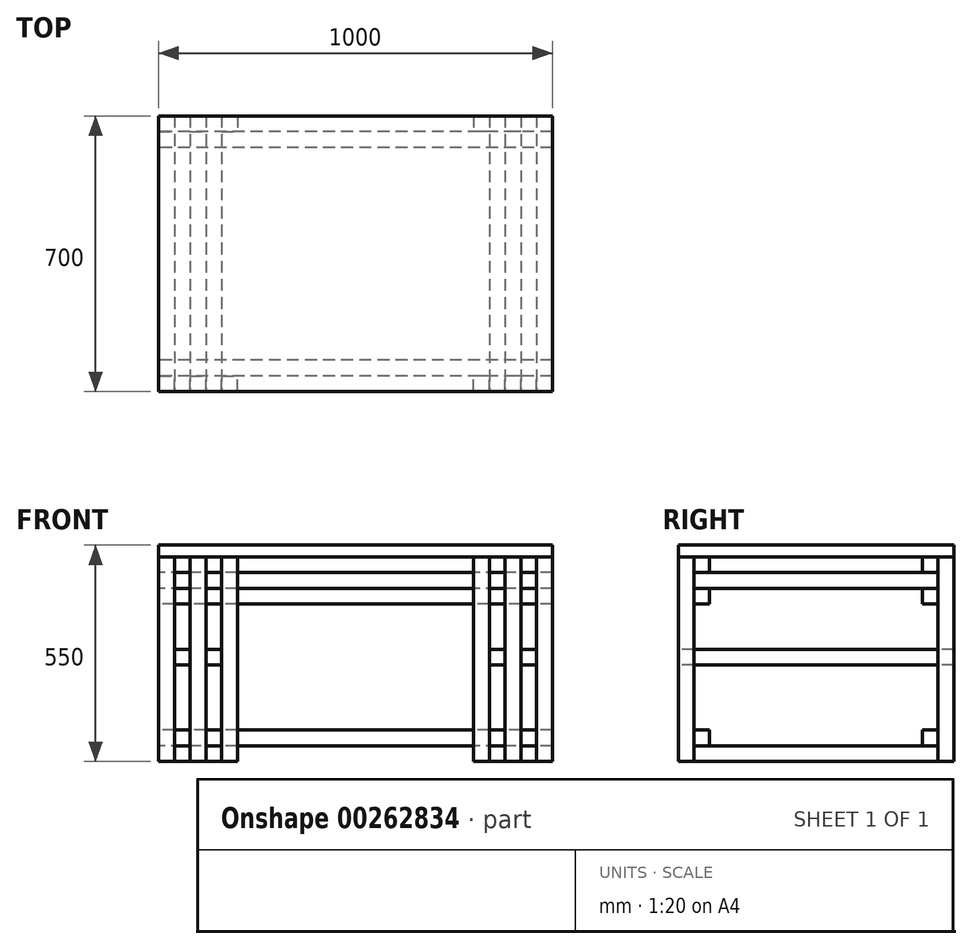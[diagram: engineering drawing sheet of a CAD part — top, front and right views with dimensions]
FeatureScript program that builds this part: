
annotation { "Feature Type Name" : "Feature", "Feature Type Description" : "" }
export const myFeature = defineFeature(function(context is Context, id is Id, definition is map)
    precondition{}
    {
        {
            var Q0;
            Q0=qCreatedBy(makeId("Top.planeOp"),FACE);
            var sketch = newSketch(context, id + "F0", { "sketchPlane" : qUnion([Q0])});
            skLineSegment(sketch, "E0.bottom", {"start": v(500, 350) * mm, "end": v(-500, 350) * mm});
            skLineSegment(sketch, "E0.top", {"start": v(500, -350) * mm, "end": v(-500, -350) * mm});
            skLineSegment(sketch, "E0.left", {"start": v(500, 350) * mm, "end": v(500, -350) * mm});
            skLineSegment(sketch, "E0.right", {"start": v(-500, 350) * mm, "end": v(-500, -350) * mm});
            skPoint(sketch, "E0.middle", {"position": v(0, 0) * mm});
            skSolve(sketch);
        }
        {
            var Q0;
            Q0=makeQuery(id+"F0.imprint","IMPRINT",FACE,{"disambiguationData":[TD([[makeQuery(id+"F0.imprint","IMPRINT",EDGE,{"derivedFrom":sQuery(id+"F0.wireOp",EDGE,"E0.bottom")}),1.0]])]});
            extrude(context, id + "F1", {"entities" : qUnion([Q0]), "depth" : 30 * mm});
        }
        {
            var Q0;
            Q0=makeQuery(id+"F1.opExtrude","CAP_FACE",FACE,{"disambiguationData":[OSD([sQuery(id+"F0.wireOp",EDGE,"E0.bottom"),sQuery(id+"F0.wireOp",EDGE,"E0.top"),sQuery(id+"F0.wireOp",EDGE,"E0.left"),sQuery(id+"F0.wireOp",EDGE,"E0.right")])],"isStart":true});
            var sketch = newSketch(context, id + "F2", { "sketchPlane" : qUnion([Q0])});
            skLineSegment(sketch, "E1.bottom", {"start": v(-500, 350) * mm, "end": v(-460, 350) * mm});
            skLineSegment(sketch, "E1.top", {"start": v(-500, 310) * mm, "end": v(-460, 310) * mm});
            skLineSegment(sketch, "E1.left", {"start": v(-500, 350) * mm, "end": v(-500, 310) * mm});
            skLineSegment(sketch, "E1.right", {"start": v(-460, 350) * mm, "end": v(-460, 310) * mm});
            skLineSegment(sketch, "E2.bottom", {"start": v(-420, 350) * mm, "end": v(-380, 350) * mm});
            skLineSegment(sketch, "E2.top", {"start": v(-420, 310) * mm, "end": v(-380, 310) * mm});
            skLineSegment(sketch, "E2.left", {"start": v(-420, 350) * mm, "end": v(-420, 310) * mm});
            skLineSegment(sketch, "E2.right", {"start": v(-380, 350) * mm, "end": v(-380, 310) * mm});
            skLineSegment(sketch, "E3.bottom", {"start": v(-340, 350) * mm, "end": v(-300, 350) * mm});
            skLineSegment(sketch, "E3.top", {"start": v(-340, 310) * mm, "end": v(-300, 310) * mm});
            skLineSegment(sketch, "E3.left", {"start": v(-340, 350) * mm, "end": v(-340, 310) * mm});
            skLineSegment(sketch, "E3.right", {"start": v(-300, 350) * mm, "end": v(-300, 310) * mm});
            skLineSegment(sketch, "E4.MirrorCS", {"start": v(420, 350) * mm, "end": v(420, 310) * mm});
            skLineSegment(sketch, "E5.MirrorCS", {"start": v(500, 350) * mm, "end": v(500, 310) * mm});
            skLineSegment(sketch, "E6.MirrorCS", {"start": v(500, 310) * mm, "end": v(460, 310) * mm});
            skLineSegment(sketch, "E7.MirrorCS", {"start": v(300, 350) * mm, "end": v(300, 310) * mm});
            skLineSegment(sketch, "E8.MirrorCS", {"start": v(340, 310) * mm, "end": v(300, 310) * mm});
            skLineSegment(sketch, "E9.MirrorCS", {"start": v(340, 350) * mm, "end": v(340, 310) * mm});
            skLineSegment(sketch, "E10.MirrorCS", {"start": v(420, 350) * mm, "end": v(380, 350) * mm});
            skLineSegment(sketch, "E11.MirrorCS", {"start": v(380, 350) * mm, "end": v(380, 310) * mm});
            skLineSegment(sketch, "E12.MirrorCS", {"start": v(340, 350) * mm, "end": v(300, 350) * mm});
            skLineSegment(sketch, "E13.MirrorCS", {"start": v(420, 310) * mm, "end": v(380, 310) * mm});
            skLineSegment(sketch, "E14.MirrorCS", {"start": v(460, 350) * mm, "end": v(460, 310) * mm});
            skLineSegment(sketch, "E15.MirrorCS", {"start": v(500, 350) * mm, "end": v(460, 350) * mm});
            skLineSegment(sketch, "E16.MirrorCS", {"start": v(-500, -350) * mm, "end": v(-500, -310) * mm});
            skLineSegment(sketch, "E17.MirrorCS", {"start": v(-420, -350) * mm, "end": v(-420, -310) * mm});
            skLineSegment(sketch, "E18.MirrorCS", {"start": v(340, -350) * mm, "end": v(300, -350) * mm});
            skLineSegment(sketch, "E19.MirrorCS", {"start": v(-500, -310) * mm, "end": v(-460, -310) * mm});
            skLineSegment(sketch, "E20.MirrorCS", {"start": v(-300, -350) * mm, "end": v(-300, -310) * mm});
            skLineSegment(sketch, "E21.MirrorCS", {"start": v(420, -310) * mm, "end": v(380, -310) * mm});
            skLineSegment(sketch, "E22.MirrorCS", {"start": v(-340, -310) * mm, "end": v(-300, -310) * mm});
            skLineSegment(sketch, "E23.MirrorCS", {"start": v(-340, -350) * mm, "end": v(-340, -310) * mm});
            skLineSegment(sketch, "E24.MirrorCS", {"start": v(420, -350) * mm, "end": v(420, -310) * mm});
            skLineSegment(sketch, "E25.MirrorCS", {"start": v(340, -310) * mm, "end": v(300, -310) * mm});
            skLineSegment(sketch, "E26.MirrorCS", {"start": v(-420, -310) * mm, "end": v(-380, -310) * mm});
            skLineSegment(sketch, "E27.MirrorCS", {"start": v(340, -350) * mm, "end": v(340, -310) * mm});
            skLineSegment(sketch, "E28.MirrorCS", {"start": v(500, -310) * mm, "end": v(460, -310) * mm});
            skLineSegment(sketch, "E29.MirrorCS", {"start": v(380, -350) * mm, "end": v(380, -310) * mm});
            skLineSegment(sketch, "E30.MirrorCS", {"start": v(300, -350) * mm, "end": v(300, -310) * mm});
            skLineSegment(sketch, "E31.MirrorCS", {"start": v(-500, -350) * mm, "end": v(-460, -350) * mm});
            skLineSegment(sketch, "E32.MirrorCS", {"start": v(-460, -350) * mm, "end": v(-460, -310) * mm});
            skLineSegment(sketch, "E33.MirrorCS", {"start": v(460, -350) * mm, "end": v(460, -310) * mm});
            skLineSegment(sketch, "E34.MirrorCS", {"start": v(500, -350) * mm, "end": v(500, -310) * mm});
            skLineSegment(sketch, "E35.MirrorCS", {"start": v(500, -350) * mm, "end": v(460, -350) * mm});
            skLineSegment(sketch, "E36.MirrorCS", {"start": v(-420, -350) * mm, "end": v(-380, -350) * mm});
            skLineSegment(sketch, "E37.MirrorCS", {"start": v(420, -350) * mm, "end": v(380, -350) * mm});
            skLineSegment(sketch, "E38.MirrorCS", {"start": v(-340, -350) * mm, "end": v(-300, -350) * mm});
            skLineSegment(sketch, "E39.MirrorCS", {"start": v(-380, -350) * mm, "end": v(-380, -310) * mm});
            skSolve(sketch);
        }
        {
            var Q0;
            Q0=makeQuery(id+"F2.imprint","IMPRINT",FACE,{"disambiguationData":[TD([[makeQuery(id+"F2.imprint","IMPRINT",EDGE,{"derivedFrom":sQuery(id+"F2.wireOp",EDGE,"E1.bottom")}),1.0]])]});
            var Q1;
            Q1=makeQuery(id+"F2.imprint","IMPRINT",FACE,{"disambiguationData":[TD([[makeQuery(id+"F2.imprint","IMPRINT",EDGE,{"derivedFrom":sQuery(id+"F2.wireOp",EDGE,"E2.bottom")}),1.0]])]});
            var Q2;
            Q2=makeQuery(id+"F2.imprint","IMPRINT",FACE,{"disambiguationData":[TD([[makeQuery(id+"F2.imprint","IMPRINT",EDGE,{"derivedFrom":sQuery(id+"F2.wireOp",EDGE,"E3.bottom")}),1.0]])]});
            var Q3;
            Q3=makeQuery(id+"F2.imprint","IMPRINT",FACE,{"disambiguationData":[TD([[makeQuery(id+"F2.imprint","IMPRINT",EDGE,{"derivedFrom":sQuery(id+"F2.wireOp",EDGE,"E7.MirrorCS")}),1.0]])]});
            var Q4;
            Q4=makeQuery(id+"F2.imprint","IMPRINT",FACE,{"disambiguationData":[TD([[makeQuery(id+"F2.imprint","IMPRINT",EDGE,{"derivedFrom":sQuery(id+"F2.wireOp",EDGE,"E4.MirrorCS")}),-1.0]])]});
            var Q5;
            Q5=makeQuery(id+"F2.imprint","IMPRINT",FACE,{"disambiguationData":[TD([[makeQuery(id+"F2.imprint","IMPRINT",EDGE,{"derivedFrom":sQuery(id+"F2.wireOp",EDGE,"E5.MirrorCS")}),1.0]])]});
            var Q6;
            Q6=makeQuery(id+"F2.imprint","IMPRINT",FACE,{"disambiguationData":[TD([[makeQuery(id+"F2.imprint","IMPRINT",EDGE,{"derivedFrom":sQuery(id+"F2.wireOp",EDGE,"E28.MirrorCS")}),1.0]])]});
            var Q7;
            Q7=makeQuery(id+"F2.imprint","IMPRINT",FACE,{"disambiguationData":[TD([[makeQuery(id+"F2.imprint","IMPRINT",EDGE,{"derivedFrom":sQuery(id+"F2.wireOp",EDGE,"E21.MirrorCS")}),1.0]])]});
            var Q8;
            Q8=makeQuery(id+"F2.imprint","IMPRINT",FACE,{"disambiguationData":[TD([[makeQuery(id+"F2.imprint","IMPRINT",EDGE,{"derivedFrom":sQuery(id+"F2.wireOp",EDGE,"E18.MirrorCS")}),-1.0]])]});
            var Q9;
            Q9=makeQuery(id+"F2.imprint","IMPRINT",FACE,{"disambiguationData":[TD([[makeQuery(id+"F2.imprint","IMPRINT",EDGE,{"derivedFrom":sQuery(id+"F2.wireOp",EDGE,"E20.MirrorCS")}),1.0]])]});
            var Q10;
            Q10=makeQuery(id+"F2.imprint","IMPRINT",FACE,{"disambiguationData":[TD([[makeQuery(id+"F2.imprint","IMPRINT",EDGE,{"derivedFrom":sQuery(id+"F2.wireOp",EDGE,"E17.MirrorCS")}),-1.0]])]});
            var Q11;
            Q11=makeQuery(id+"F2.imprint","IMPRINT",FACE,{"disambiguationData":[TD([[makeQuery(id+"F2.imprint","IMPRINT",EDGE,{"derivedFrom":sQuery(id+"F2.wireOp",EDGE,"E16.MirrorCS")}),-1.0]])]});
            extrude(context, id + "F3", {"entities" : qUnion([Q0, Q1, Q2, Q3, Q4, Q5, Q6, Q7, Q8, Q9, Q10, Q11]), "depth" : 520 * mm});
        }
        {
            var Q0;
            Q0=makeQuery(id+"F1.opExtrude","SWEPT_FACE",FACE,{"disambiguationData":[OSD([sQuery(id+"F0.wireOp",EDGE,"E0.top")])]});
            var sketch = newSketch(context, id + "F4", { "sketchPlane" : qUnion([Q0])});
            skLineSegment(sketch, "E40", {"start": v(-689.3, -40) * mm, "end": v(694.23, -40) * mm, "construction": true});
            skLineSegment(sketch, "E41", {"start": v(-703.3, -480) * mm, "end": v(680.23, -480) * mm, "construction": true});
            skLineSegment(sketch, "E42.bottom", {"start": v(-460, -40) * mm, "end": v(-420, -40) * mm});
            skLineSegment(sketch, "E42.top", {"start": v(-460, -80) * mm, "end": v(-420, -80) * mm});
            skLineSegment(sketch, "E42.left", {"start": v(-460, -40) * mm, "end": v(-460, -80) * mm});
            skLineSegment(sketch, "E42.right", {"start": v(-420, -40) * mm, "end": v(-420, -80) * mm});
            skLineSegment(sketch, "E43.bottom", {"start": v(-380, -40) * mm, "end": v(-340, -40) * mm});
            skLineSegment(sketch, "E43.top", {"start": v(-380, -80) * mm, "end": v(-340, -80) * mm});
            skLineSegment(sketch, "E43.left", {"start": v(-380, -40) * mm, "end": v(-380, -80) * mm});
            skLineSegment(sketch, "E43.right", {"start": v(-340, -40) * mm, "end": v(-340, -80) * mm});
            skLineSegment(sketch, "E44.bottom", {"start": v(-460, -480) * mm, "end": v(-420, -480) * mm});
            skLineSegment(sketch, "E44.top", {"start": v(-460, -520) * mm, "end": v(-420, -520) * mm});
            skLineSegment(sketch, "E44.left", {"start": v(-460, -480) * mm, "end": v(-460, -520) * mm});
            skLineSegment(sketch, "E44.right", {"start": v(-420, -480) * mm, "end": v(-420, -520) * mm});
            skLineSegment(sketch, "E45.bottom", {"start": v(-380, -480) * mm, "end": v(-340, -480) * mm});
            skLineSegment(sketch, "E45.top", {"start": v(-380, -520) * mm, "end": v(-340, -520) * mm});
            skLineSegment(sketch, "E45.left", {"start": v(-380, -480) * mm, "end": v(-380, -520) * mm});
            skLineSegment(sketch, "E45.right", {"start": v(-340, -480) * mm, "end": v(-340, -520) * mm});
            skLineSegment(sketch, "E46.MirrorCS", {"start": v(340, -480) * mm, "end": v(340, -520) * mm});
            skLineSegment(sketch, "E47.MirrorCS", {"start": v(460, -480) * mm, "end": v(460, -520) * mm});
            skLineSegment(sketch, "E48.MirrorCS", {"start": v(380, -480) * mm, "end": v(380, -520) * mm});
            skLineSegment(sketch, "E49.MirrorCS", {"start": v(420, -480) * mm, "end": v(420, -520) * mm});
            skLineSegment(sketch, "E50.MirrorCS", {"start": v(380, -480) * mm, "end": v(340, -480) * mm});
            skLineSegment(sketch, "E51.MirrorCS", {"start": v(420, -40) * mm, "end": v(420, -80) * mm});
            skLineSegment(sketch, "E52.MirrorCS", {"start": v(380, -40) * mm, "end": v(340, -40) * mm});
            skLineSegment(sketch, "E53.MirrorCS", {"start": v(380, -80) * mm, "end": v(340, -80) * mm});
            skLineSegment(sketch, "E54.MirrorCS", {"start": v(340, -40) * mm, "end": v(340, -80) * mm});
            skLineSegment(sketch, "E55.MirrorCS", {"start": v(460, -480) * mm, "end": v(420, -480) * mm});
            skLineSegment(sketch, "E56.MirrorCS", {"start": v(460, -80) * mm, "end": v(420, -80) * mm});
            skLineSegment(sketch, "E57.MirrorCS", {"start": v(380, -40) * mm, "end": v(380, -80) * mm});
            skLineSegment(sketch, "E58.MirrorCS", {"start": v(460, -40) * mm, "end": v(460, -80) * mm});
            skLineSegment(sketch, "E59.MirrorCS", {"start": v(460, -40) * mm, "end": v(420, -40) * mm});
            skLineSegment(sketch, "E60.MirrorCS", {"start": v(460, -520) * mm, "end": v(420, -520) * mm});
            skLineSegment(sketch, "E61.MirrorCS", {"start": v(380, -520) * mm, "end": v(340, -520) * mm});
            skLineSegment(sketch, "E62", {"start": v(-683.27, -235) * mm, "end": v(699.88, -235) * mm, "construction": true});
            skLineSegment(sketch, "E63", {"start": v(-688.83, -275) * mm, "end": v(699.88, -275) * mm, "construction": true});
            skLineSegment(sketch, "E64.bottom", {"start": v(-460, -235) * mm, "end": v(-420, -235) * mm});
            skLineSegment(sketch, "E64.top", {"start": v(-460, -275) * mm, "end": v(-420, -275) * mm});
            skLineSegment(sketch, "E64.left", {"start": v(-460, -235) * mm, "end": v(-460, -275) * mm});
            skLineSegment(sketch, "E64.right", {"start": v(-420, -235) * mm, "end": v(-420, -275) * mm});
            skLineSegment(sketch, "E65.bottom", {"start": v(-380, -235) * mm, "end": v(-340, -235) * mm});
            skLineSegment(sketch, "E65.top", {"start": v(-380, -275) * mm, "end": v(-340, -275) * mm});
            skLineSegment(sketch, "E65.left", {"start": v(-380, -235) * mm, "end": v(-380, -275) * mm});
            skLineSegment(sketch, "E65.right", {"start": v(-340, -235) * mm, "end": v(-340, -275) * mm});
            skLineSegment(sketch, "E66.MirrorCS", {"start": v(380, -235) * mm, "end": v(380, -275) * mm});
            skLineSegment(sketch, "E67.MirrorCS", {"start": v(380, -275) * mm, "end": v(340, -275) * mm});
            skLineSegment(sketch, "E68.MirrorCS", {"start": v(460, -275) * mm, "end": v(420, -275) * mm});
            skLineSegment(sketch, "E69.MirrorCS", {"start": v(420, -235) * mm, "end": v(420, -275) * mm});
            skLineSegment(sketch, "E70.MirrorCS", {"start": v(460, -235) * mm, "end": v(460, -275) * mm});
            skLineSegment(sketch, "E71.MirrorCS", {"start": v(380, -235) * mm, "end": v(340, -235) * mm});
            skLineSegment(sketch, "E72.MirrorCS", {"start": v(340, -235) * mm, "end": v(340, -275) * mm});
            skLineSegment(sketch, "E73.MirrorCS", {"start": v(460, -235) * mm, "end": v(420, -235) * mm});
            skSolve(sketch);
        }
        {
            var Q0;
            Q0=makeQuery(id+"F4.imprint","IMPRINT",FACE,{"disambiguationData":[TD([[makeQuery(id+"F4.imprint","IMPRINT",EDGE,{"derivedFrom":sQuery(id+"F4.wireOp",EDGE,"E42.bottom")}),-1.0]])]});
            var Q1;
            Q1=makeQuery(id+"F4.imprint","IMPRINT",FACE,{"disambiguationData":[TD([[makeQuery(id+"F4.imprint","IMPRINT",EDGE,{"derivedFrom":sQuery(id+"F4.wireOp",EDGE,"E43.bottom")}),-1.0]])]});
            var Q2;
            Q2=makeQuery(id+"F4.imprint","IMPRINT",FACE,{"disambiguationData":[TD([[makeQuery(id+"F4.imprint","IMPRINT",EDGE,{"derivedFrom":sQuery(id+"F4.wireOp",EDGE,"E45.bottom")}),-1.0]])]});
            var Q3;
            Q3=makeQuery(id+"F4.imprint","IMPRINT",FACE,{"disambiguationData":[TD([[makeQuery(id+"F4.imprint","IMPRINT",EDGE,{"derivedFrom":sQuery(id+"F4.wireOp",EDGE,"E44.bottom")}),-1.0]])]});
            var Q4;
            Q4=makeQuery(id+"F4.imprint","IMPRINT",FACE,{"disambiguationData":[TD([[makeQuery(id+"F4.imprint","IMPRINT",EDGE,{"derivedFrom":sQuery(id+"F4.wireOp",EDGE,"E52.MirrorCS")}),1.0]])]});
            var Q5;
            Q5=makeQuery(id+"F4.imprint","IMPRINT",FACE,{"disambiguationData":[TD([[makeQuery(id+"F4.imprint","IMPRINT",EDGE,{"derivedFrom":sQuery(id+"F4.wireOp",EDGE,"E51.MirrorCS")}),1.0]])]});
            var Q6;
            Q6=makeQuery(id+"F4.imprint","IMPRINT",FACE,{"disambiguationData":[TD([[makeQuery(id+"F4.imprint","IMPRINT",EDGE,{"derivedFrom":sQuery(id+"F4.wireOp",EDGE,"E47.MirrorCS")}),-1.0]])]});
            var Q7;
            Q7=makeQuery(id+"F4.imprint","IMPRINT",FACE,{"disambiguationData":[TD([[makeQuery(id+"F4.imprint","IMPRINT",EDGE,{"derivedFrom":sQuery(id+"F4.wireOp",EDGE,"E46.MirrorCS")}),1.0]])]});
            extrude(context, id + "F5", {"entities" : qUnion([Q0, Q1, Q2, Q3, Q4, Q5, Q6, Q7]), "oppositeDirection" : true, "depth" : 700 * mm});
        }
        {
            var Q0;
            Q0=makeQuery(id+"F1.opExtrude","SWEPT_FACE",FACE,{"disambiguationData":[OSD([sQuery(id+"F0.wireOp",EDGE,"E0.right")])]});
            var sketch = newSketch(context, id + "F6", { "sketchPlane" : qUnion([Q0])});
            skLineSegment(sketch, "E74", {"start": v(-398.8, -40) * mm, "end": v(418.11, -40) * mm, "construction": true});
            skLineSegment(sketch, "E75", {"start": v(-398.8, -480) * mm, "end": v(436.07, -480) * mm, "construction": true});
            skLineSegment(sketch, "E76", {"start": v(-392.73, -80) * mm, "end": v(423.7, -80) * mm, "construction": true});
            skLineSegment(sketch, "E77.bottom", {"start": v(-310, 0) * mm, "end": v(-270, 0) * mm});
            skLineSegment(sketch, "E77.top", {"start": v(-310, -40) * mm, "end": v(-270, -40) * mm});
            skLineSegment(sketch, "E77.left", {"start": v(-310, 0) * mm, "end": v(-310, -40) * mm});
            skLineSegment(sketch, "E77.right", {"start": v(-270, 0) * mm, "end": v(-270, -40) * mm});
            skLineSegment(sketch, "E78.bottom", {"start": v(-310, -80) * mm, "end": v(-270, -80) * mm});
            skLineSegment(sketch, "E78.top", {"start": v(-310, -120) * mm, "end": v(-270, -120) * mm});
            skLineSegment(sketch, "E78.left", {"start": v(-310, -80) * mm, "end": v(-310, -120) * mm});
            skLineSegment(sketch, "E78.right", {"start": v(-270, -80) * mm, "end": v(-270, -120) * mm});
            skLineSegment(sketch, "E79.bottom", {"start": v(-310, -440) * mm, "end": v(-270, -440) * mm});
            skLineSegment(sketch, "E79.top", {"start": v(-310, -480) * mm, "end": v(-270, -480) * mm});
            skLineSegment(sketch, "E79.left", {"start": v(-310, -440) * mm, "end": v(-310, -480) * mm});
            skLineSegment(sketch, "E79.right", {"start": v(-270, -440) * mm, "end": v(-270, -480) * mm});
            skLineSegment(sketch, "E80", {"start": v(-270, 64.27) * mm, "end": v(-270, -568.68) * mm, "construction": true});
            skLineSegment(sketch, "E81.MirrorCS", {"start": v(310, -480) * mm, "end": v(270, -480) * mm});
            skLineSegment(sketch, "E82.MirrorCS", {"start": v(310, -440) * mm, "end": v(270, -440) * mm});
            skLineSegment(sketch, "E83.MirrorCS", {"start": v(270, -80) * mm, "end": v(270, -120) * mm});
            skLineSegment(sketch, "E84.MirrorCS", {"start": v(310, -80) * mm, "end": v(310, -120) * mm});
            skLineSegment(sketch, "E85.MirrorCS", {"start": v(310, -440) * mm, "end": v(310, -480) * mm});
            skLineSegment(sketch, "E86.MirrorCS", {"start": v(270, -440) * mm, "end": v(270, -480) * mm});
            skLineSegment(sketch, "E87.MirrorCS", {"start": v(270, 0) * mm, "end": v(270, -40) * mm});
            skLineSegment(sketch, "E88.MirrorCS", {"start": v(310, -40) * mm, "end": v(270, -40) * mm});
            skLineSegment(sketch, "E89.MirrorCS", {"start": v(310, 0) * mm, "end": v(310, -40) * mm});
            skLineSegment(sketch, "E90.MirrorCS", {"start": v(310, 0) * mm, "end": v(270, 0) * mm});
            skLineSegment(sketch, "E91.MirrorCS", {"start": v(310, -120) * mm, "end": v(270, -120) * mm});
            skLineSegment(sketch, "E92.MirrorCS", {"start": v(310, -80) * mm, "end": v(270, -80) * mm});
            skSolve(sketch);
        }
        {
            var Q0;
            Q0=makeQuery(id+"F6.imprint","IMPRINT",FACE,{"disambiguationData":[TD([[makeQuery(id+"F6.imprint","IMPRINT",EDGE,{"derivedFrom":sQuery(id+"F6.wireOp",EDGE,"E77.bottom")}),-1.0]])]});
            var Q1;
            Q1=makeQuery(id+"F6.imprint","IMPRINT",FACE,{"disambiguationData":[TD([[makeQuery(id+"F6.imprint","IMPRINT",EDGE,{"derivedFrom":sQuery(id+"F6.wireOp",EDGE,"E78.bottom")}),-1.0]])]});
            var Q2;
            Q2=makeQuery(id+"F6.imprint","IMPRINT",FACE,{"disambiguationData":[TD([[makeQuery(id+"F6.imprint","IMPRINT",EDGE,{"derivedFrom":sQuery(id+"F6.wireOp",EDGE,"E79.bottom")}),-1.0]])]});
            var Q3;
            Q3=makeQuery(id+"F6.imprint","IMPRINT",FACE,{"disambiguationData":[TD([[makeQuery(id+"F6.imprint","IMPRINT",EDGE,{"derivedFrom":sQuery(id+"F6.wireOp",EDGE,"E87.MirrorCS")}),1.0]])]});
            var Q4;
            Q4=makeQuery(id+"F6.imprint","IMPRINT",FACE,{"disambiguationData":[TD([[makeQuery(id+"F6.imprint","IMPRINT",EDGE,{"derivedFrom":sQuery(id+"F6.wireOp",EDGE,"E83.MirrorCS")}),1.0]])]});
            var Q5;
            Q5=makeQuery(id+"F6.imprint","IMPRINT",FACE,{"disambiguationData":[TD([[makeQuery(id+"F6.imprint","IMPRINT",EDGE,{"derivedFrom":sQuery(id+"F6.wireOp",EDGE,"E81.MirrorCS")}),-1.0]])]});
            extrude(context, id + "F7", {"entities" : qUnion([Q0, Q1, Q2, Q3, Q4, Q5]), "flatOperationType" : FlatOperationType.REMOVE, "oppositeDirection" : true, "offsetDistance" : 25 * mm, "depth" : 1000 * mm, "domain" : OperationDomain.MODEL});
        }
        {
            var Q0;
            Q0=makeQuery(id+"F4.imprint","IMPRINT",FACE,{"disambiguationData":[TD([[makeQuery(id+"F4.imprint","IMPRINT",EDGE,{"derivedFrom":sQuery(id+"F4.wireOp",EDGE,"E64.bottom")}),-1.0]])]});
            var Q1;
            Q1=makeQuery(id+"F4.imprint","IMPRINT",FACE,{"disambiguationData":[TD([[makeQuery(id+"F4.imprint","IMPRINT",EDGE,{"derivedFrom":sQuery(id+"F4.wireOp",EDGE,"E65.bottom")}),-1.0]])]});
            var Q2;
            Q2=makeQuery(id+"F4.imprint","IMPRINT",FACE,{"disambiguationData":[TD([[makeQuery(id+"F4.imprint","IMPRINT",EDGE,{"derivedFrom":sQuery(id+"F4.wireOp",EDGE,"E66.MirrorCS")}),-1.0]])]});
            var Q3;
            Q3=makeQuery(id+"F4.imprint","IMPRINT",FACE,{"disambiguationData":[TD([[makeQuery(id+"F4.imprint","IMPRINT",EDGE,{"derivedFrom":sQuery(id+"F4.wireOp",EDGE,"E68.MirrorCS")}),-1.0]])]});
            extrude(context, id + "F8", {"entities" : qUnion([Q0, Q1, Q2, Q3]), "oppositeDirection" : true, "depth" : 700 * mm});
        }
    });
